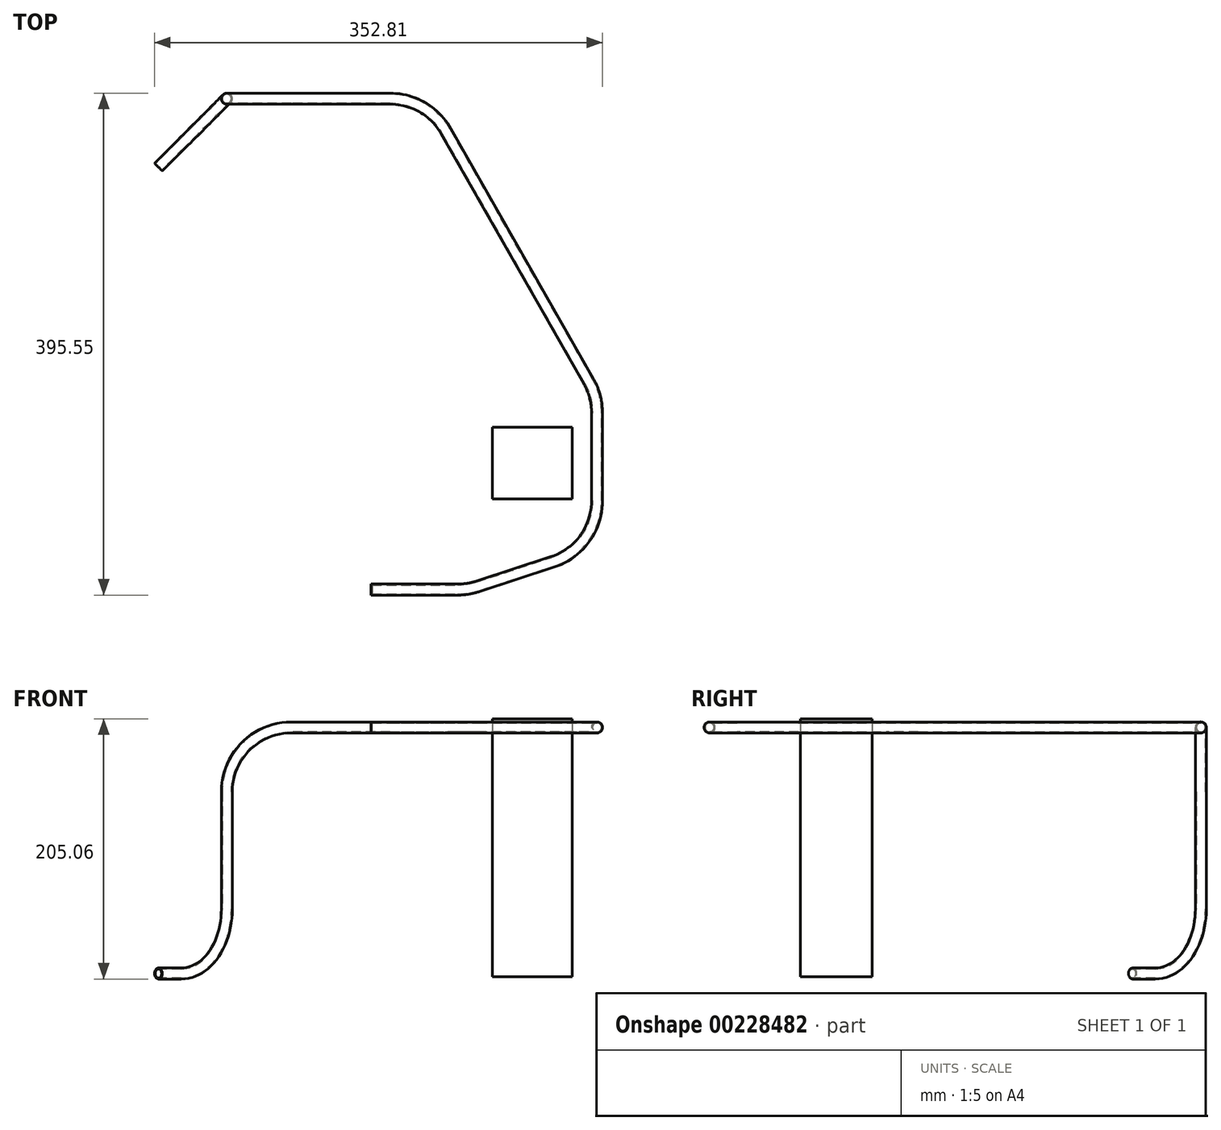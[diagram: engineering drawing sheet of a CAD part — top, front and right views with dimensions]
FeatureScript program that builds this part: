
annotation { "Feature Type Name" : "Feature", "Feature Type Description" : "" }
export const myFeature = defineFeature(function(context is Context, id is Id, definition is map)
    precondition{}
    {
        {
            var Q0;
            Q0=qCreatedBy(makeId("Top.planeOp"),FACE);
            var sketch = newSketch(context, id + "F0", { "sketchPlane" : qUnion([Q0])});
            skLineSegment(sketch, "E0", {"start": v(0, 0) * mm, "end": v(308.08, 0) * mm});
            skLineSegment(sketch, "E1", {"start": v(308.08, 0) * mm, "end": v(308.08, -99.9) * mm});
            skLineSegment(sketch, "E2", {"start": v(308.08, -99.9) * mm, "end": v(333.48, -99.9) * mm});
            skLineSegment(sketch, "E3", {"start": v(0, 0) * mm, "end": v(140.48, 0) * mm});
            skLineSegment(sketch, "E4", {"start": v(140.48, 0) * mm, "end": v(140.48, 233.1) * mm});
            skLineSegment(sketch, "E5", {"start": v(140.48, 233.1) * mm, "end": v(165.88, 233.1) * mm});
            skLineSegment(sketch, "E6", {"start": v(0, 0) * mm, "end": v(466.34, 0) * mm});
            skLineSegment(sketch, "E7", {"start": v(466.34, 0) * mm, "end": v(466.34, -28.43) * mm});
            skLineSegment(sketch, "E8", {"start": v(466.34, -28.43) * mm, "end": v(491.74, -28.43) * mm});
            skLineSegment(sketch, "E9", {"start": v(0, 0) * mm, "end": v(403.6, 0) * mm});
            skLineSegment(sketch, "E10", {"start": v(403.6, 0) * mm, "end": v(403.6, 27.96) * mm});
            skLineSegment(sketch, "E11", {"start": v(403.6, 27.96) * mm, "end": v(429, 27.96) * mm});
            skSolve(sketch);
        }
        {
            var Q0;
            Q0=sQuery(id+"F0.wireOp",EDGE,"E2");
            cPlane(context, id + "F1", {"entities" : qUnion([Q0]), "cplaneType" : CPlaneType.LINE_ANGLE, "offset" : 25.4 * mm, "angle" : 0 * degree, "width" : 152.4 * mm, "height" : 152.4 * mm});
        }
        {
            var Q0;
            Q0=sQuery(id+"F0.wireOp",EDGE,"E8");
            cPlane(context, id + "F2", {"entities" : qUnion([Q0]), "cplaneType" : CPlaneType.LINE_ANGLE, "offset" : 25.4 * mm, "angle" : 0 * degree, "width" : 152.4 * mm, "height" : 152.4 * mm});
        }
        {
            var Q0;
            Q0=sQuery(id+"F0.wireOp",EDGE,"E11");
            cPlane(context, id + "F3", {"entities" : qUnion([Q0]), "cplaneType" : CPlaneType.LINE_ANGLE, "offset" : 25.4 * mm, "angle" : 0 * degree, "width" : 152.4 * mm, "height" : 152.4 * mm});
        }
        {
            var Q0;
            Q0=sQuery(id+"F0.wireOp",EDGE,"E5");
            cPlane(context, id + "F4", {"entities" : qUnion([Q0]), "cplaneType" : CPlaneType.LINE_ANGLE, "offset" : 25.4 * mm, "angle" : 0 * degree, "width" : 152.4 * mm, "height" : 152.4 * mm});
        }
        {
            var Q0;
            Q0=qCreatedBy(id+"F2.planeOp",FACE);
            var sketch = newSketch(context, id + "F5", { "sketchPlane" : qUnion([Q0])});
            skLineSegment(sketch, "E12", {"start": v(-466.34, 0) * mm, "end": v(-466.34, 772.24) * mm});
            skLineSegment(sketch, "E13", {"start": v(-466.34, 772.24) * mm, "end": v(-440.94, 772.24) * mm});
            skSolve(sketch);
        }
        {
            var Q0;
            Q0=qCreatedBy(id+"F3.planeOp",FACE);
            var sketch = newSketch(context, id + "F6", { "sketchPlane" : qUnion([Q0])});
            skLineSegment(sketch, "E14", {"start": v(-403.6, 0) * mm, "end": v(-403.6, 772.24) * mm});
            skLineSegment(sketch, "E15", {"start": v(-403.6, 772.24) * mm, "end": v(-378.2, 772.24) * mm});
            skSolve(sketch);
        }
        {
            var Q0;
            Q0=qCreatedBy(id+"F1.planeOp",FACE);
            var sketch = newSketch(context, id + "F7", { "sketchPlane" : qUnion([Q0])});
            skLineSegment(sketch, "E16", {"start": v(-308.08, 0) * mm, "end": v(-308.08, 968.64) * mm});
            skLineSegment(sketch, "E17", {"start": v(-308.08, 968.64) * mm, "end": v(-333.48, 968.64) * mm});
            skSolve(sketch);
        }
        {
            var Q0;
            Q0=qCreatedBy(id+"F4.planeOp",FACE);
            var sketch = newSketch(context, id + "F8", { "sketchPlane" : qUnion([Q0])});
            skLineSegment(sketch, "E18", {"start": v(-140.48, 0) * mm, "end": v(-140.48, 774.72) * mm});
            skLineSegment(sketch, "E19", {"start": v(-140.48, 774.72) * mm, "end": v(-115.08, 774.72) * mm});
            skSolve(sketch);
        }
        {
            var Q0;
            Q0=sQuery(id+"F5.wireOp",EDGE,"E13");
            cPlane(context, id + "F9", {"entities" : qUnion([Q0]), "cplaneType" : CPlaneType.LINE_ANGLE, "offset" : 25.4 * mm, "angle" : 90 * degree, "width" : 152.4 * mm, "height" : 152.4 * mm});
        }
        {
            var Q0;
            Q0=qCreatedBy(id+"F9.planeOp",FACE);
            var sketch = newSketch(context, id + "F10", { "sketchPlane" : qUnion([Q0])});
            skLineSegment(sketch, "E20.bottom", {"start": v(466.34, -28.43) * mm, "end": v(403.6, -28.43) * mm});
            skLineSegment(sketch, "E20.top", {"start": v(466.34, 27.96) * mm, "end": v(403.6, 27.96) * mm});
            skLineSegment(sketch, "E20.left", {"start": v(466.34, -28.43) * mm, "end": v(466.34, 27.96) * mm});
            skLineSegment(sketch, "E20.right", {"start": v(403.6, -28.43) * mm, "end": v(403.6, 27.96) * mm});
            skSolve(sketch);
        }
        {
            var Q0;
            Q0 = qSketchRegion(id + "F10", true);
            extrude(context, id + "F11", {"entities" : qUnion([Q0]), "depth" : 203.2 * mm});
        }
        {
            var Q0;
            Q0=sQuery(id+"F8.wireOp",EDGE,"E19");
            cPlane(context, id + "F12", {"entities" : qUnion([Q0]), "cplaneType" : CPlaneType.LINE_ANGLE, "offset" : 25.4 * mm, "angle" : 90 * degree, "width" : 152.4 * mm, "height" : 152.4 * mm});
        }
        {
            var Q0;
            Q0=qCreatedBy(id+"F12.planeOp",FACE);
            var sketch = newSketch(context, id + "F13", { "sketchPlane" : qUnion([Q0])});
            skLineSegment(sketch, "E21", {"start": v(140.48, 233.1) * mm, "end": v(73.87, 299.7) * mm});
            skSolve(sketch);
        }
        {
            var Q0;
            Q0=sQuery(id+"F13.wireOp",EDGE,"E21");
            cPlane(context, id + "F14", {"entities" : qUnion([Q0]), "cplaneType" : CPlaneType.LINE_ANGLE, "offset" : 25.4 * mm, "angle" : 90 * degree, "width" : 152.4 * mm, "height" : 152.4 * mm});
        }
        {
            var Q0;
            Q0=qCreatedBy(id+"F14.planeOp",FACE);
            var sketch = newSketch(context, id + "F15", { "sketchPlane" : qUnion([Q0])});
            skCircle(sketch, "E22", {"center": v(65.5, 774.72) * mm, "radius": 4.34 * mm});
            skSolve(sketch);
        }
        {
            var Q0;
            Q0=sQuery(id+"F7.wireOp",EDGE,"E16");
            cPlane(context, id + "F16", {"entities" : qUnion([Q0]), "cplaneType" : CPlaneType.LINE_ANGLE, "offset" : 25.4 * mm, "angle" : 0 * degree, "width" : 152.4 * mm, "height" : 152.4 * mm});
        }
        {
            var Q0;
            Q0=qCreatedBy(id+"F16.planeOp",FACE);
            var sketch = newSketch(context, id + "F17", { "sketchPlane" : qUnion([Q0])});
            skCircle(sketch, "E23", {"center": v(-99.9, 968.64) * mm, "radius": 4.34 * mm});
            skSolve(sketch);
        }
        {
            var Q0;
            Q0=qCreatedBy(id+"F12.planeOp",FACE);
            var sketch = newSketch(context, id + "F18", { "sketchPlane" : qUnion([Q0])});
            skLineSegment(sketch, "E24", {"start": v(140.48, 233.1) * mm, "end": v(194.36, 286.98) * mm});
            skSolve(sketch);
        }
        {
            var Q0;
            Q0=sQuery(id+"F7.wireOp",EDGE,"E17");
            cPlane(context, id + "F19", {"entities" : qUnion([Q0]), "cplaneType" : CPlaneType.LINE_ANGLE, "offset" : 25.4 * mm, "angle" : 90 * degree, "width" : 152.4 * mm, "height" : 152.4 * mm});
        }
        {
            var Q0;
            Q0=qCreatedBy(id+"F19.planeOp",FACE);
            var sketch = newSketch(context, id + "F20", { "sketchPlane" : qUnion([Q0])});
            skLineSegment(sketch, "E25", {"start": v(308.08, -99.9) * mm, "end": v(384.28, -99.9) * mm});
            skLineSegment(sketch, "E26", {"start": v(384.28, -99.9) * mm, "end": v(450.86, -78.14) * mm});
            skLineSegment(sketch, "E27", {"start": v(485.88, -29.85) * mm, "end": v(485.88, 39.28) * mm});
            skLineSegment(sketch, "E28", {"start": v(479.22, 64.43) * mm, "end": v(367.05, 261.33) * mm});
            skLineSegment(sketch, "E29", {"start": v(322.91, 286.98) * mm, "end": v(194.36, 286.98) * mm});
            skLineSegment(sketch, "E30", {"start": v(384.28, -99.9) * mm, "end": v(384.28, -66.7) * mm});
            skLineSegment(sketch, "E31", {"start": v(384.28, -66.7) * mm, "end": v(485.88, -66.7) * mm});
            skPoint(sketch, "E32.visualSharp", {"position": v(485.88, -66.7) * mm});
            skArc(sketch, "E32.filletArc", {"start": v(450.86, -78.14) * mm, "mid": v(476.2, -59.67) * mm, "end": v(485.88, -29.85) * mm});
            skPoint(sketch, "E33.visualSharp", {"position": v(485.88, 52.74) * mm});
            skArc(sketch, "E33.filletArc", {"start": v(485.88, 39.28) * mm, "mid": v(484.2, 52.3) * mm, "end": v(479.22, 64.43) * mm});
            skPoint(sketch, "E34.visualSharp", {"position": v(352.44, 286.98) * mm});
            skArc(sketch, "E34.filletArc", {"start": v(367.05, 261.33) * mm, "mid": v(348.44, 280.1) * mm, "end": v(322.91, 286.98) * mm});
            skSolve(sketch);
        }
        {
            var Q0;
            Q0=sQuery(id+"F20.wireOp",VERTEX,"E29.start");
            var Q1;
            Q1=sQuery(id+"F20.wireOp",VERTEX,"E29.end");
            var Q2;
            Q2=sQuery(id+"F18.wireOp",VERTEX,"E24.end");
            cPlane(context, id + "F21", {"entities" : qUnion([Q0, Q1, Q2]), "cplaneType" : CPlaneType.THREE_POINT, "offset" : 25.4 * mm, "width" : 152.4 * mm, "height" : 152.4 * mm});
        }
        {
            var Q0;
            Q0=qCreatedBy(id+"F21.planeOp",FACE);
            var sketch = newSketch(context, id + "F22", { "sketchPlane" : qUnion([Q0])});
            skLineSegment(sketch, "E35", {"start": v(-245.16, 968.64) * mm, "end": v(-322.91, 968.64) * mm});
            skLineSegment(sketch, "E36", {"start": v(-194.36, 917.84) * mm, "end": v(-194.36, 774.72) * mm});
            skPoint(sketch, "E37.visualSharp", {"position": v(-194.36, 968.64) * mm});
            skArc(sketch, "E37.filletArc", {"start": v(-194.36, 917.84) * mm, "mid": v(-209.24, 953.77) * mm, "end": v(-245.16, 968.64) * mm});
            skSolve(sketch);
        }
        {
            var Q0;
            Q0=sQuery(id+"F18.wireOp",EDGE,"E24");
            var Q1;
            Q1=sQuery(id+"F22.wireOp",EDGE,"E36");
            cPlane(context, id + "F23", {"entities" : qUnion([Q0, Q1]), "cplaneType" : CPlaneType.LINE_ANGLE, "offset" : 25.4 * mm, "angle" : 0 * degree, "width" : 152.4 * mm, "height" : 152.4 * mm});
        }
        {
            var Q0;
            Q0=qCreatedBy(id+"F23.planeOp",FACE);
            var sketch = newSketch(context, id + "F24", { "sketchPlane" : qUnion([Q0])});
            skLineSegment(sketch, "E38", {"start": v(-264.16, 774.72) * mm, "end": v(-289.56, 774.72) * mm});
            skLineSegment(sketch, "E39", {"start": v(-340.36, 825.52) * mm, "end": v(-340.36, 917.84) * mm});
            skPoint(sketch, "E40.visualSharp", {"position": v(-340.36, 774.72) * mm});
            skArc(sketch, "E40.filletArc", {"start": v(-340.36, 825.52) * mm, "mid": v(-325.48, 789.6) * mm, "end": v(-289.56, 774.72) * mm});
            skSolve(sketch);
        }
        {
            var Q0;
            Q0=sQuery(id+"F20.wireOp",EDGE,"E26");
            var Q1;
            Q1=sQuery(id+"F20.wireOp",EDGE,"E25");
            cPlane(context, id + "F25", {"entities" : qUnion([Q0, Q1]), "cplaneType" : CPlaneType.LINE_ANGLE, "offset" : 25.4 * mm, "angle" : 0 * degree, "width" : 152.4 * mm, "height" : 152.4 * mm});
        }
        {
            var Q0;
            Q0=qCreatedBy(id+"F25.planeOp",FACE);
            var sketch = newSketch(context, id + "F26", { "sketchPlane" : qUnion([Q0])});
            skLineSegment(sketch, "E41", {"start": v(376.2, 99.9) * mm, "end": v(308.08, 99.9) * mm});
            skLineSegment(sketch, "E42", {"start": v(391.97, 97.38) * mm, "end": v(450.86, 78.14) * mm});
            skPoint(sketch, "E43.visualSharp", {"position": v(384.28, 99.9) * mm});
            skArc(sketch, "E43.filletArc", {"start": v(391.97, 97.38) * mm, "mid": v(384.18, 99.26) * mm, "end": v(376.2, 99.9) * mm});
            skSolve(sketch);
        }
        {
            var Q0;
            Q0=makeQuery(id+"F17.imprint","IMPRINT",FACE,{"disambiguationData":[TD([[makeQuery(id+"F17.imprint","IMPRINT",EDGE,{"derivedFrom":sQuery(id+"F17.wireOp",EDGE,"E23")}),1.0]])]});
            var Q1;
            Q1=sQuery(id+"F26.wireOp",EDGE,"E41");
            var Q2;
            Q2=sQuery(id+"F26.wireOp",EDGE,"E43.filletArc");
            var Q3;
            Q3=sQuery(id+"F26.wireOp",EDGE,"E42");
            var Q4;
            Q4=sQuery(id+"F20.wireOp",EDGE,"E32.filletArc");
            var Q5;
            Q5=sQuery(id+"F20.wireOp",EDGE,"E27");
            var Q6;
            Q6=sQuery(id+"F20.wireOp",EDGE,"E33.filletArc");
            var Q7;
            Q7=sQuery(id+"F20.wireOp",EDGE,"E28");
            var Q8;
            Q8=sQuery(id+"F20.wireOp",EDGE,"E34.filletArc");
            var Q9;
            Q9=sQuery(id+"F22.wireOp",EDGE,"E35");
            var Q10;
            Q10=sQuery(id+"F22.wireOp",EDGE,"E37.filletArc");
            var Q11;
            Q11=sQuery(id+"F24.wireOp",EDGE,"E39");
            var Q12;
            Q12=sQuery(id+"F24.wireOp",EDGE,"E40.filletArc");
            var Q13;
            Q13=sQuery(id+"F24.wireOp",EDGE,"E38");
            sweep(context, id + "F27", {"profiles" : qUnion([Q0]), "path" : qUnion([Q1, Q2, Q3, Q4, Q5, Q6, Q7, Q8, Q9, Q10, Q11, Q12, Q13])});
        }
        {
            var Q0;
            Q0=makeQuery(id+"F27.opSweep","CAP_FACE",FACE,{"disambiguationData":[OSD([sQuery(id+"F17.wireOp",EDGE,"E23"),sQuery(id+"F24.wireOp",VERTEX,"E38.start")])],"isStart":false});
            shell(context, id + "F28", {"entities" : qUnion([Q0]), "thickness" : 0.76 * mm});
        }
    });
